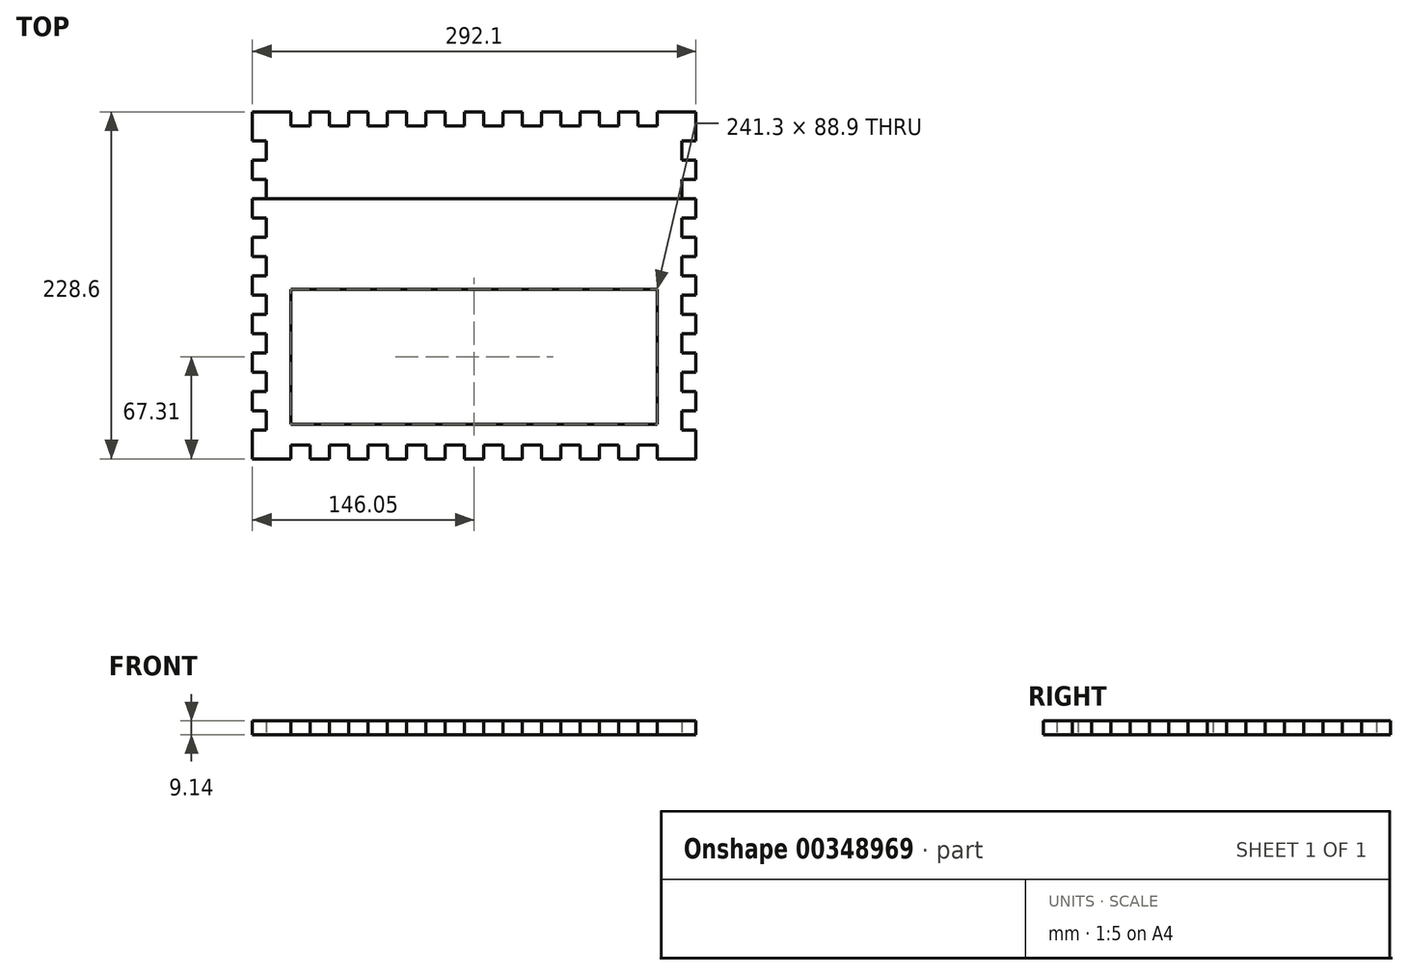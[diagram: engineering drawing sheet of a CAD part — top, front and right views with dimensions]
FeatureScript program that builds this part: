
annotation { "Feature Type Name" : "Feature", "Feature Type Description" : "" }
export const myFeature = defineFeature(function(context is Context, id is Id, definition is map)
    precondition{}
    {
        {
            var Q0;
            Q0=qCreatedBy(makeId("Top.planeOp"),FACE);
            var sketch = newSketch(context, id + "F0", { "sketchPlane" : qUnion([Q0])});
            skLineSegment(sketch, "E0.bottom", {"start": v(0, 0) * mm, "end": v(25.4, 0) * mm});
            skLineSegment(sketch, "E0.left", {"start": v(0, 0) * mm, "end": v(0, -19.05) * mm});
            skLineSegment(sketch, "E1", {"start": v(25.4, 0) * mm, "end": v(25.4, -9.14) * mm});
            skLineSegment(sketch, "E2", {"start": v(25.4, -9.14) * mm, "end": v(38.1, -9.14) * mm});
            skLineSegment(sketch, "E3", {"start": v(38.1, -9.14) * mm, "end": v(38.1, 0) * mm});
            skLineSegment(sketch, "E4", {"start": v(38.1, 0) * mm, "end": v(50.8, 0) * mm});
            skLineSegment(sketch, "E5", {"start": v(50.8, 0) * mm, "end": v(50.8, -9.14) * mm});
            skLineSegment(sketch, "E6", {"start": v(50.8, -9.14) * mm, "end": v(63.5, -9.14) * mm});
            skLineSegment(sketch, "E7", {"start": v(63.5, -9.14) * mm, "end": v(63.5, 0) * mm});
            skLineSegment(sketch, "E8", {"start": v(63.5, 0) * mm, "end": v(76.2, 0) * mm});
            skLineSegment(sketch, "E9", {"start": v(76.2, 0) * mm, "end": v(76.2, -9.14) * mm});
            skLineSegment(sketch, "E10", {"start": v(76.2, -9.14) * mm, "end": v(88.9, -9.14) * mm});
            skLineSegment(sketch, "E11", {"start": v(88.9, -9.14) * mm, "end": v(88.9, 0) * mm});
            skLineSegment(sketch, "E12.trimOffspring", {"start": v(88.9, 0) * mm, "end": v(101.6, 0) * mm});
            skLineSegment(sketch, "E13", {"start": v(101.6, 0) * mm, "end": v(101.6, -9.14) * mm});
            skLineSegment(sketch, "E14", {"start": v(101.6, -9.14) * mm, "end": v(114.3, -9.14) * mm});
            skLineSegment(sketch, "E15", {"start": v(114.3, -9.14) * mm, "end": v(114.3, 0) * mm});
            skLineSegment(sketch, "E16", {"start": v(114.3, 0) * mm, "end": v(127, 0) * mm});
            skLineSegment(sketch, "E17", {"start": v(127, 0) * mm, "end": v(127, -9.14) * mm});
            skLineSegment(sketch, "E18", {"start": v(127, -9.14) * mm, "end": v(139.7, -9.14) * mm});
            skLineSegment(sketch, "E19", {"start": v(139.7, -9.14) * mm, "end": v(139.7, 0) * mm});
            skLineSegment(sketch, "E20.trimOffspring", {"start": v(139.7, 0) * mm, "end": v(152.4, 0) * mm});
            skLineSegment(sketch, "E21", {"start": v(152.4, 0) * mm, "end": v(152.4, -9.14) * mm});
            skLineSegment(sketch, "E22", {"start": v(152.4, -9.14) * mm, "end": v(165.1, -9.14) * mm});
            skLineSegment(sketch, "E23", {"start": v(165.1, -9.14) * mm, "end": v(165.1, 0) * mm});
            skLineSegment(sketch, "E24", {"start": v(165.1, 0) * mm, "end": v(177.8, 0) * mm});
            skLineSegment(sketch, "E25", {"start": v(177.8, 0) * mm, "end": v(177.8, -9.14) * mm});
            skLineSegment(sketch, "E26", {"start": v(177.8, -9.14) * mm, "end": v(190.5, -9.14) * mm});
            skLineSegment(sketch, "E27", {"start": v(190.5, -9.14) * mm, "end": v(190.5, 0) * mm});
            skLineSegment(sketch, "E28", {"start": v(190.5, 0) * mm, "end": v(203.2, 0) * mm});
            skLineSegment(sketch, "E29", {"start": v(203.2, 0) * mm, "end": v(203.2, -9.14) * mm});
            skLineSegment(sketch, "E30", {"start": v(203.2, -9.14) * mm, "end": v(215.9, -9.14) * mm});
            skLineSegment(sketch, "E31", {"start": v(215.9, -9.14) * mm, "end": v(215.9, 0) * mm});
            skLineSegment(sketch, "E32.trimOffspring", {"start": v(215.9, 0) * mm, "end": v(228.6, 0) * mm});
            skLineSegment(sketch, "E33", {"start": v(228.6, 0) * mm, "end": v(228.6, -9.14) * mm});
            skLineSegment(sketch, "E34", {"start": v(228.6, -9.14) * mm, "end": v(241.3, -9.14) * mm});
            skLineSegment(sketch, "E35", {"start": v(241.3, -9.14) * mm, "end": v(241.3, 0) * mm});
            skLineSegment(sketch, "E36", {"start": v(241.3, 0) * mm, "end": v(254, 0) * mm});
            skLineSegment(sketch, "E37", {"start": v(254, 0) * mm, "end": v(254, -9.14) * mm});
            skLineSegment(sketch, "E38", {"start": v(254, -9.14) * mm, "end": v(266.7, -9.14) * mm});
            skLineSegment(sketch, "E39", {"start": v(266.7, -9.14) * mm, "end": v(266.7, 0) * mm});
            skLineSegment(sketch, "E40.trimOffspring", {"start": v(266.7, 0) * mm, "end": v(292.1, 0) * mm});
            skLineSegment(sketch, "E41", {"start": v(0, -19.05) * mm, "end": v(9.14, -19.05) * mm});
            skLineSegment(sketch, "E42", {"start": v(9.14, -19.05) * mm, "end": v(9.14, -31.75) * mm});
            skLineSegment(sketch, "E43", {"start": v(9.14, -31.75) * mm, "end": v(0, -31.75) * mm});
            skLineSegment(sketch, "E44", {"start": v(0, -31.75) * mm, "end": v(0, -44.45) * mm});
            skLineSegment(sketch, "E45", {"start": v(0, -44.45) * mm, "end": v(9.14, -44.45) * mm});
            skLineSegment(sketch, "E46", {"start": v(9.14, -44.45) * mm, "end": v(9.14, -57.15) * mm});
            skLineSegment(sketch, "E47", {"start": v(9.14, -57.15) * mm, "end": v(0, -57.15) * mm});
            skLineSegment(sketch, "E48", {"start": v(0, -57.15) * mm, "end": v(0, -69.85) * mm});
            skLineSegment(sketch, "E49", {"start": v(0, -69.85) * mm, "end": v(9.14, -69.85) * mm});
            skLineSegment(sketch, "E50", {"start": v(9.14, -69.85) * mm, "end": v(9.14, -82.55) * mm});
            skLineSegment(sketch, "E51", {"start": v(9.14, -82.55) * mm, "end": v(0, -82.55) * mm});
            skLineSegment(sketch, "E52.trimOffspring", {"start": v(0, -82.55) * mm, "end": v(0, -95.25) * mm});
            skLineSegment(sketch, "E53", {"start": v(0, -95.25) * mm, "end": v(9.14, -95.25) * mm});
            skLineSegment(sketch, "E54", {"start": v(9.14, -95.25) * mm, "end": v(9.14, -107.95) * mm});
            skLineSegment(sketch, "E55", {"start": v(9.14, -107.95) * mm, "end": v(0, -107.95) * mm});
            skLineSegment(sketch, "E56", {"start": v(0, -107.95) * mm, "end": v(0, -120.65) * mm});
            skLineSegment(sketch, "E57", {"start": v(0, -120.65) * mm, "end": v(9.14, -120.65) * mm});
            skLineSegment(sketch, "E58", {"start": v(9.14, -120.65) * mm, "end": v(9.14, -133.35) * mm});
            skLineSegment(sketch, "E59", {"start": v(9.14, -133.35) * mm, "end": v(0, -133.35) * mm});
            skLineSegment(sketch, "E60.trimOffspring", {"start": v(0, -133.35) * mm, "end": v(0, -146.05) * mm});
            skLineSegment(sketch, "E61", {"start": v(0, -146.05) * mm, "end": v(9.14, -146.05) * mm});
            skLineSegment(sketch, "E62", {"start": v(9.14, -146.05) * mm, "end": v(9.14, -158.75) * mm});
            skLineSegment(sketch, "E63", {"start": v(9.14, -158.75) * mm, "end": v(0, -158.75) * mm});
            skLineSegment(sketch, "E64", {"start": v(0, -158.75) * mm, "end": v(0, -171.45) * mm});
            skLineSegment(sketch, "E65", {"start": v(0, -171.45) * mm, "end": v(9.14, -171.45) * mm});
            skLineSegment(sketch, "E66", {"start": v(9.14, -171.45) * mm, "end": v(9.14, -184.15) * mm});
            skLineSegment(sketch, "E67", {"start": v(9.14, -184.15) * mm, "end": v(0, -184.15) * mm});
            skLineSegment(sketch, "E68.trimOffspring", {"start": v(0, -184.15) * mm, "end": v(0, -196.85) * mm});
            skLineSegment(sketch, "E69", {"start": v(0, -196.85) * mm, "end": v(9.14, -196.85) * mm});
            skLineSegment(sketch, "E70", {"start": v(9.14, -196.85) * mm, "end": v(9.14, -209.55) * mm});
            skLineSegment(sketch, "E71", {"start": v(9.14, -209.55) * mm, "end": v(0, -209.55) * mm});
            skLineSegment(sketch, "E72.trimOffspring", {"start": v(0, -209.55) * mm, "end": v(0, -228.6) * mm});
            skLineSegment(sketch, "E73", {"start": v(146.05, 0) * mm, "end": v(146.05, -205.74) * mm, "construction": true});
            skLineSegment(sketch, "E74.MirrorCS", {"start": v(292.1, 0) * mm, "end": v(292.1, -19.05) * mm});
            skLineSegment(sketch, "E75.MirrorCS", {"start": v(292.1, -19.05) * mm, "end": v(282.96, -19.05) * mm});
            skLineSegment(sketch, "E76.MirrorCS", {"start": v(282.96, -19.05) * mm, "end": v(282.96, -31.75) * mm});
            skLineSegment(sketch, "E77.MirrorCS", {"start": v(282.96, -31.75) * mm, "end": v(292.1, -31.75) * mm});
            skLineSegment(sketch, "E78.MirrorCS", {"start": v(292.1, -31.75) * mm, "end": v(292.1, -44.45) * mm});
            skLineSegment(sketch, "E79.MirrorCS", {"start": v(292.1, -44.45) * mm, "end": v(282.96, -44.45) * mm});
            skLineSegment(sketch, "E80.MirrorCS", {"start": v(282.96, -44.45) * mm, "end": v(282.96, -57.15) * mm});
            skLineSegment(sketch, "E81.MirrorCS", {"start": v(282.96, -57.15) * mm, "end": v(292.1, -57.15) * mm});
            skLineSegment(sketch, "E82.MirrorCS", {"start": v(292.1, -57.15) * mm, "end": v(292.1, -69.85) * mm});
            skLineSegment(sketch, "E83.MirrorCS", {"start": v(292.1, -69.85) * mm, "end": v(282.96, -69.85) * mm});
            skLineSegment(sketch, "E84.MirrorCS", {"start": v(282.96, -69.85) * mm, "end": v(282.96, -82.55) * mm});
            skLineSegment(sketch, "E85.MirrorCS", {"start": v(282.96, -82.55) * mm, "end": v(292.1, -82.55) * mm});
            skLineSegment(sketch, "E86.MirrorCS", {"start": v(292.1, -82.55) * mm, "end": v(292.1, -95.25) * mm});
            skLineSegment(sketch, "E87.MirrorCS", {"start": v(292.1, -95.25) * mm, "end": v(282.96, -95.25) * mm});
            skLineSegment(sketch, "E88.MirrorCS", {"start": v(282.96, -95.25) * mm, "end": v(282.96, -107.95) * mm});
            skLineSegment(sketch, "E89.MirrorCS", {"start": v(282.96, -107.95) * mm, "end": v(292.1, -107.95) * mm});
            skLineSegment(sketch, "E90.MirrorCS", {"start": v(292.1, -107.95) * mm, "end": v(292.1, -120.65) * mm});
            skLineSegment(sketch, "E91.MirrorCS", {"start": v(292.1, -120.65) * mm, "end": v(282.96, -120.65) * mm});
            skLineSegment(sketch, "E92.MirrorCS", {"start": v(282.96, -120.65) * mm, "end": v(282.96, -133.35) * mm});
            skLineSegment(sketch, "E93.MirrorCS", {"start": v(282.96, -133.35) * mm, "end": v(292.1, -133.35) * mm});
            skLineSegment(sketch, "E94.MirrorCS", {"start": v(292.1, -133.35) * mm, "end": v(292.1, -146.05) * mm});
            skLineSegment(sketch, "E95.MirrorCS", {"start": v(292.1, -146.05) * mm, "end": v(282.96, -146.05) * mm});
            skLineSegment(sketch, "E96.MirrorCS", {"start": v(282.96, -146.05) * mm, "end": v(282.96, -158.75) * mm});
            skLineSegment(sketch, "E97.MirrorCS", {"start": v(282.96, -158.75) * mm, "end": v(292.1, -158.75) * mm});
            skLineSegment(sketch, "E98.MirrorCS", {"start": v(292.1, -158.75) * mm, "end": v(292.1, -171.45) * mm});
            skLineSegment(sketch, "E99.MirrorCS", {"start": v(292.1, -171.45) * mm, "end": v(282.96, -171.45) * mm});
            skLineSegment(sketch, "E100.MirrorCS", {"start": v(282.96, -171.45) * mm, "end": v(282.96, -184.15) * mm});
            skLineSegment(sketch, "E101.MirrorCS", {"start": v(282.96, -184.15) * mm, "end": v(292.1, -184.15) * mm});
            skLineSegment(sketch, "E102.MirrorCS", {"start": v(292.1, -184.15) * mm, "end": v(292.1, -196.85) * mm});
            skLineSegment(sketch, "E103.MirrorCS", {"start": v(292.1, -196.85) * mm, "end": v(282.96, -196.85) * mm});
            skLineSegment(sketch, "E104.MirrorCS", {"start": v(282.96, -196.85) * mm, "end": v(282.96, -209.55) * mm});
            skLineSegment(sketch, "E105.MirrorCS", {"start": v(282.96, -209.55) * mm, "end": v(292.1, -209.55) * mm});
            skLineSegment(sketch, "E106.MirrorCS", {"start": v(292.1, -209.55) * mm, "end": v(292.1, -228.6) * mm});
            skLineSegment(sketch, "E107", {"start": v(0, -114.3) * mm, "end": v(292.1, -114.3) * mm, "construction": true});
            skLineSegment(sketch, "E108.MirrorCS", {"start": v(0, -228.6) * mm, "end": v(25.4, -228.6) * mm});
            skLineSegment(sketch, "E109.MirrorCS", {"start": v(25.4, -228.6) * mm, "end": v(25.4, -219.46) * mm});
            skLineSegment(sketch, "E110.MirrorCS", {"start": v(25.4, -219.46) * mm, "end": v(38.1, -219.46) * mm});
            skLineSegment(sketch, "E111.MirrorCS", {"start": v(38.1, -228.6) * mm, "end": v(50.8, -228.6) * mm});
            skLineSegment(sketch, "E112.MirrorCS", {"start": v(50.8, -228.6) * mm, "end": v(50.8, -219.46) * mm});
            skLineSegment(sketch, "E113.MirrorCS", {"start": v(50.8, -219.46) * mm, "end": v(63.5, -219.46) * mm});
            skLineSegment(sketch, "E114.MirrorCS", {"start": v(63.5, -228.6) * mm, "end": v(76.2, -228.6) * mm});
            skLineSegment(sketch, "E115.MirrorCS", {"start": v(76.2, -219.46) * mm, "end": v(88.9, -219.46) * mm});
            skLineSegment(sketch, "E116.MirrorCS", {"start": v(76.2, -228.6) * mm, "end": v(76.2, -219.46) * mm});
            skLineSegment(sketch, "E117.MirrorCS", {"start": v(88.9, -228.6) * mm, "end": v(101.6, -228.6) * mm});
            skLineSegment(sketch, "E118.MirrorCS", {"start": v(101.6, -228.6) * mm, "end": v(101.6, -219.46) * mm});
            skLineSegment(sketch, "E119.MirrorCS", {"start": v(101.6, -219.46) * mm, "end": v(114.3, -219.46) * mm});
            skLineSegment(sketch, "E120.MirrorCS", {"start": v(114.3, -219.46) * mm, "end": v(114.3, -228.6) * mm});
            skLineSegment(sketch, "E121.MirrorCS", {"start": v(114.3, -228.6) * mm, "end": v(127, -228.6) * mm});
            skLineSegment(sketch, "E122.MirrorCS", {"start": v(127, -228.6) * mm, "end": v(127, -219.46) * mm});
            skLineSegment(sketch, "E123.MirrorCS", {"start": v(127, -219.46) * mm, "end": v(139.7, -219.46) * mm});
            skLineSegment(sketch, "E124.MirrorCS", {"start": v(139.7, -228.6) * mm, "end": v(152.4, -228.6) * mm});
            skLineSegment(sketch, "E125.MirrorCS", {"start": v(152.4, -228.6) * mm, "end": v(152.4, -219.46) * mm});
            skLineSegment(sketch, "E126.MirrorCS", {"start": v(152.4, -219.46) * mm, "end": v(165.1, -219.46) * mm});
            skLineSegment(sketch, "E127.MirrorCS", {"start": v(165.1, -219.46) * mm, "end": v(165.1, -228.6) * mm});
            skLineSegment(sketch, "E128.MirrorCS", {"start": v(165.1, -228.6) * mm, "end": v(177.8, -228.6) * mm});
            skLineSegment(sketch, "E129.MirrorCS", {"start": v(177.8, -228.6) * mm, "end": v(177.8, -219.46) * mm});
            skLineSegment(sketch, "E130.MirrorCS", {"start": v(177.8, -219.46) * mm, "end": v(190.5, -219.46) * mm});
            skLineSegment(sketch, "E131.MirrorCS", {"start": v(190.5, -219.46) * mm, "end": v(190.5, -228.6) * mm});
            skLineSegment(sketch, "E132.MirrorCS", {"start": v(190.5, -228.6) * mm, "end": v(203.2, -228.6) * mm});
            skLineSegment(sketch, "E133.MirrorCS", {"start": v(203.2, -228.6) * mm, "end": v(203.2, -219.46) * mm});
            skLineSegment(sketch, "E134.MirrorCS", {"start": v(203.2, -219.46) * mm, "end": v(215.9, -219.46) * mm});
            skLineSegment(sketch, "E135.MirrorCS", {"start": v(215.9, -219.46) * mm, "end": v(215.9, -228.6) * mm});
            skLineSegment(sketch, "E136.MirrorCS", {"start": v(215.9, -228.6) * mm, "end": v(228.6, -228.6) * mm});
            skLineSegment(sketch, "E137.MirrorCS", {"start": v(38.1, -219.46) * mm, "end": v(38.1, -228.6) * mm});
            skLineSegment(sketch, "E138.MirrorCS", {"start": v(63.5, -219.46) * mm, "end": v(63.5, -228.6) * mm});
            skLineSegment(sketch, "E139.MirrorCS", {"start": v(88.9, -219.46) * mm, "end": v(88.9, -228.6) * mm});
            skLineSegment(sketch, "E140.MirrorCS", {"start": v(139.7, -219.46) * mm, "end": v(139.7, -228.6) * mm});
            skLineSegment(sketch, "E141.MirrorCS", {"start": v(228.6, -228.6) * mm, "end": v(228.6, -219.46) * mm});
            skLineSegment(sketch, "E142.MirrorCS", {"start": v(228.6, -219.46) * mm, "end": v(241.3, -219.46) * mm});
            skLineSegment(sketch, "E143.MirrorCS", {"start": v(241.3, -219.46) * mm, "end": v(241.3, -228.6) * mm});
            skLineSegment(sketch, "E144.MirrorCS", {"start": v(241.3, -228.6) * mm, "end": v(254, -228.6) * mm});
            skLineSegment(sketch, "E145.MirrorCS", {"start": v(254, -228.6) * mm, "end": v(254, -219.46) * mm});
            skLineSegment(sketch, "E146.MirrorCS", {"start": v(254, -219.46) * mm, "end": v(266.7, -219.46) * mm});
            skLineSegment(sketch, "E147.MirrorCS", {"start": v(266.7, -219.46) * mm, "end": v(266.7, -228.6) * mm});
            skLineSegment(sketch, "E148.MirrorCS", {"start": v(266.7, -228.6) * mm, "end": v(292.1, -228.6) * mm});
            skLineSegment(sketch, "E149", {"start": v(9.14, -57.15) * mm, "end": v(282.96, -57.15) * mm});
            skLineSegment(sketch, "E150.bottom", {"start": v(25.4, -116.84) * mm, "end": v(266.7, -116.84) * mm});
            skLineSegment(sketch, "E150.top", {"start": v(25.4, -205.74) * mm, "end": v(266.7, -205.74) * mm});
            skLineSegment(sketch, "E150.left", {"start": v(25.4, -116.84) * mm, "end": v(25.4, -205.74) * mm});
            skLineSegment(sketch, "E150.right", {"start": v(266.7, -116.84) * mm, "end": v(266.7, -205.74) * mm});
            skSolve(sketch);
        }
        {
            var Q0;
            Q0=makeQuery(id+"F0.imprint","IMPRINT",FACE,{"disambiguationData":[TD([[makeQuery(id+"F0.imprint","IMPRINT",EDGE,{"derivedFrom":sQuery(id+"F0.wireOp",EDGE,"E0.bottom")}),-1.0]])]});
            extrude(context, id + "F1", {"entities" : qUnion([Q0]), "depth" : 9.14 * mm});
        }
        {
            var Q0;
            Q0=makeQuery(id+"F0.imprint","IMPRINT",FACE,{"disambiguationData":[TD([[makeQuery(id+"F0.imprint","IMPRINT",EDGE,{"derivedFrom":sQuery(id+"F0.wireOp",EDGE,"E47")}),1.0]])]});
            extrude(context, id + "F2", {"entities" : qUnion([Q0]), "depth" : 9.14 * mm});
        }
    });
